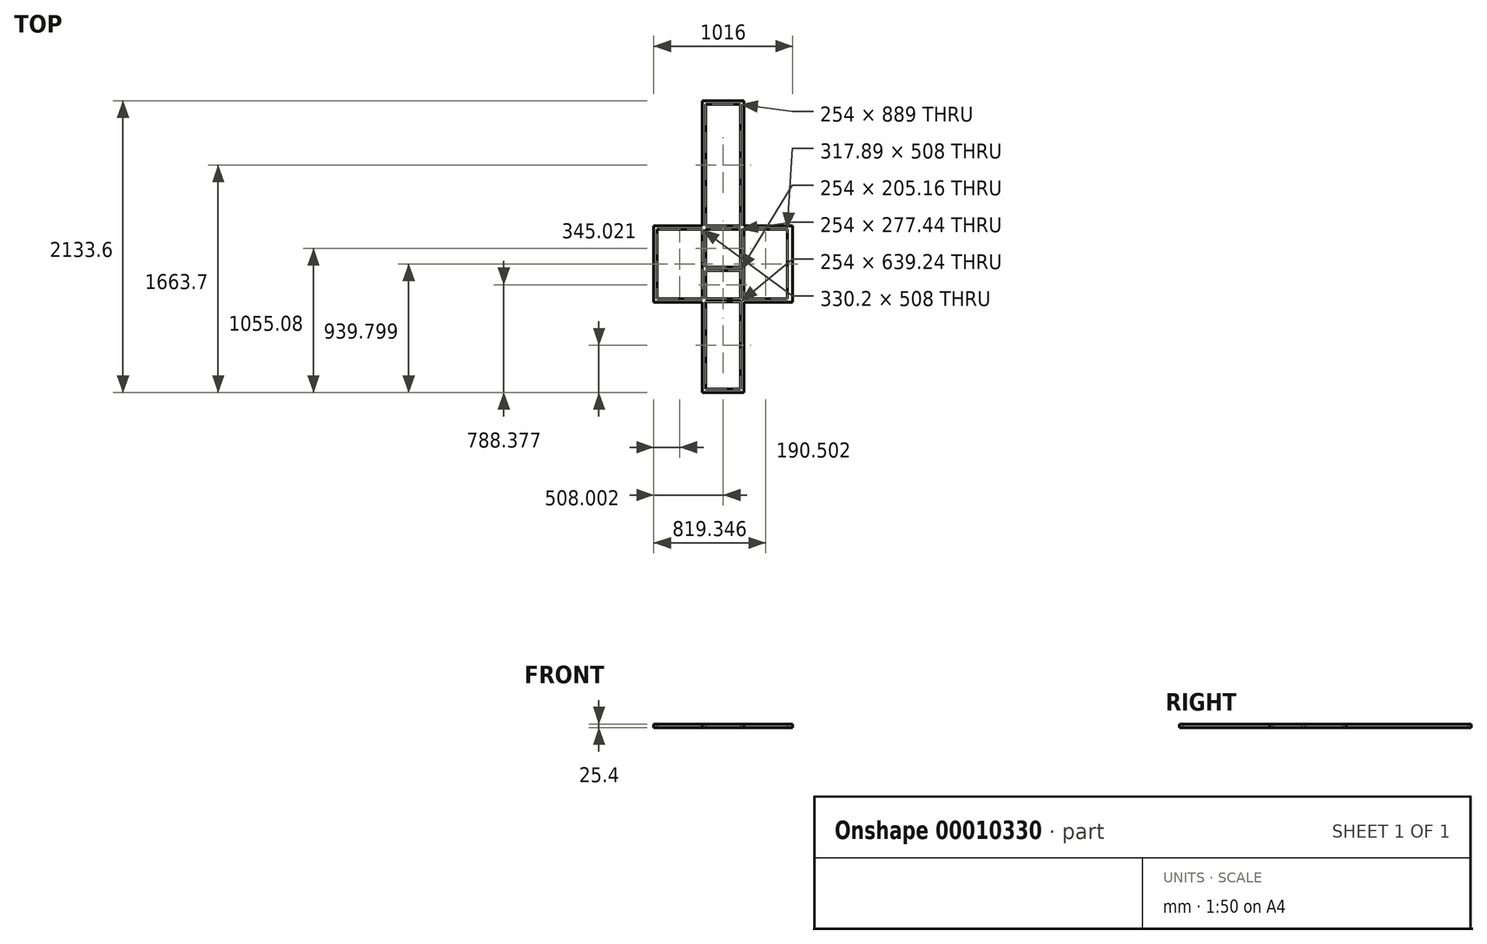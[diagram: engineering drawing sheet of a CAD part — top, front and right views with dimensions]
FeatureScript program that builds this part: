
annotation { "Feature Type Name" : "Feature", "Feature Type Description" : "" }
export const myFeature = defineFeature(function(context is Context, id is Id, definition is map)
    precondition{}
    {
        {
            var Q0;
            Q0=qCreatedBy(makeId("Top.planeOp"),FACE);
            var sketch = newSketch(context, id + "F0", { "sketchPlane" : qUnion([Q0])});
            skLineSegment(sketch, "E0", {"start": v(-138.29, -1372.67) * mm, "end": v(166.51, -1372.67) * mm});
            skLineSegment(sketch, "E1", {"start": v(166.51, -1372.67) * mm, "end": v(166.51, -712.27) * mm});
            skLineSegment(sketch, "E2", {"start": v(166.51, -712.27) * mm, "end": v(522.11, -712.27) * mm});
            skLineSegment(sketch, "E3", {"start": v(522.11, -712.27) * mm, "end": v(522.11, -153.47) * mm});
            skLineSegment(sketch, "E4", {"start": v(522.11, -153.47) * mm, "end": v(166.51, -153.47) * mm});
            skLineSegment(sketch, "E5", {"start": v(166.51, -153.47) * mm, "end": v(166.51, 760.93) * mm});
            skLineSegment(sketch, "E6", {"start": v(166.51, 760.93) * mm, "end": v(-138.29, 760.93) * mm});
            skLineSegment(sketch, "E7", {"start": v(-138.29, 760.93) * mm, "end": v(-138.29, -153.47) * mm});
            skLineSegment(sketch, "E8", {"start": v(-138.29, -153.47) * mm, "end": v(-493.89, -153.47) * mm});
            skLineSegment(sketch, "E9", {"start": v(-138.29, -1372.67) * mm, "end": v(-138.29, -712.27) * mm});
            skLineSegment(sketch, "E10", {"start": v(-138.29, -712.27) * mm, "end": v(-493.89, -712.27) * mm});
            skLineSegment(sketch, "E11", {"start": v(-493.89, -712.27) * mm, "end": v(-493.89, -153.47) * mm});
            skLineSegment(sketch, "E12.bottom", {"start": v(-468.49, -178.87) * mm, "end": v(-138.29, -178.87) * mm});
            skLineSegment(sketch, "E12.top", {"start": v(-468.49, -686.87) * mm, "end": v(-138.29, -686.87) * mm});
            skLineSegment(sketch, "E12.left", {"start": v(-468.49, -178.87) * mm, "end": v(-468.49, -686.87) * mm});
            skLineSegment(sketch, "E12.right", {"start": v(-138.29, -178.87) * mm, "end": v(-138.29, -686.87) * mm});
            skLineSegment(sketch, "E13.bottom", {"start": v(-112.89, -708.03) * mm, "end": v(141.11, -708.03) * mm});
            skLineSegment(sketch, "E13.top", {"start": v(-112.89, -1347.27) * mm, "end": v(141.11, -1347.27) * mm});
            skLineSegment(sketch, "E13.left", {"start": v(-112.89, -708.03) * mm, "end": v(-112.89, -1347.27) * mm});
            skLineSegment(sketch, "E13.right", {"start": v(141.11, -708.03) * mm, "end": v(141.11, -1347.27) * mm});
            skLineSegment(sketch, "E14.bottom", {"start": v(-112.89, -153.47) * mm, "end": v(141.11, -153.47) * mm});
            skLineSegment(sketch, "E14.top", {"start": v(-112.89, 735.53) * mm, "end": v(141.11, 735.53) * mm});
            skLineSegment(sketch, "E14.left", {"start": v(-112.89, -153.47) * mm, "end": v(-112.89, 735.53) * mm});
            skLineSegment(sketch, "E14.right", {"start": v(141.11, -153.47) * mm, "end": v(141.11, 735.53) * mm});
            skLineSegment(sketch, "E15.bottom", {"start": v(-112.89, -178.87) * mm, "end": v(141.11, -178.87) * mm});
            skLineSegment(sketch, "E15.top", {"start": v(-112.89, -456.32) * mm, "end": v(141.11, -456.32) * mm});
            skLineSegment(sketch, "E15.left", {"start": v(-112.89, -178.87) * mm, "end": v(-112.89, -456.32) * mm});
            skLineSegment(sketch, "E15.right", {"start": v(141.11, -178.87) * mm, "end": v(141.11, -456.32) * mm});
            skLineSegment(sketch, "E16.bottom", {"start": v(-112.89, -481.72) * mm, "end": v(141.11, -481.72) * mm});
            skLineSegment(sketch, "E16.top", {"start": v(-112.89, -686.87) * mm, "end": v(141.11, -686.87) * mm});
            skLineSegment(sketch, "E16.left", {"start": v(-112.89, -481.72) * mm, "end": v(-112.89, -686.87) * mm});
            skLineSegment(sketch, "E16.right", {"start": v(141.11, -481.72) * mm, "end": v(141.11, -686.87) * mm});
            skLineSegment(sketch, "E17.bottom", {"start": v(166.51, -178.87) * mm, "end": v(484.4, -178.87) * mm});
            skLineSegment(sketch, "E17.top", {"start": v(166.51, -686.87) * mm, "end": v(484.4, -686.87) * mm});
            skLineSegment(sketch, "E17.left", {"start": v(166.51, -178.87) * mm, "end": v(166.51, -686.87) * mm});
            skLineSegment(sketch, "E17.right", {"start": v(484.4, -178.87) * mm, "end": v(484.4, -686.87) * mm});
            skSolve(sketch);
        }
        {
            var Q0;
            Q0 = qSketchRegion(id + "F0", true);
            extrude(context, id + "F1", {"entities" : qUnion([Q0]), "depth" : 25.4 * mm});
        }
    });
